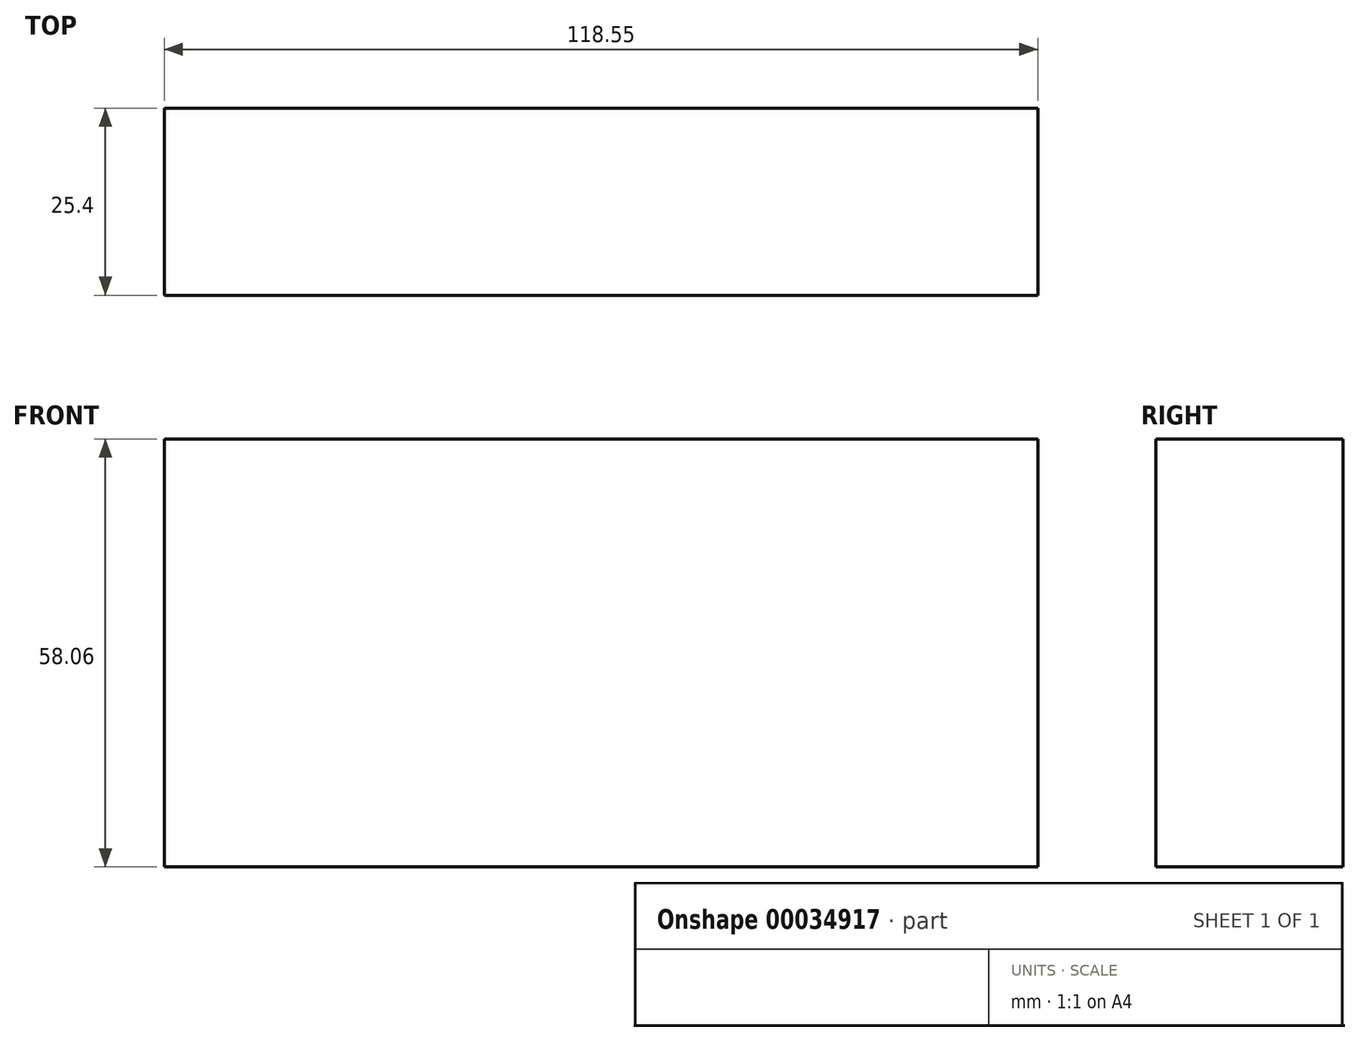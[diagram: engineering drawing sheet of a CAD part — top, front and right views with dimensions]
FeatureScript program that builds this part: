
annotation { "Feature Type Name" : "Feature", "Feature Type Description" : "" }
export const myFeature = defineFeature(function(context is Context, id is Id, definition is map)
    precondition{}
    {
        {
            var Q0;
            Q0=qCreatedBy(makeId("Front.planeOp"),FACE);
            var sketch = newSketch(context, id + "F0", { "sketchPlane" : qUnion([Q0])});
            skLineSegment(sketch, "E0.bottom", {"start": v(-55.41, 34.59) * mm, "end": v(63.14, 34.59) * mm});
            skLineSegment(sketch, "E0.top", {"start": v(-55.41, -23.47) * mm, "end": v(63.14, -23.47) * mm});
            skLineSegment(sketch, "E0.left", {"start": v(-55.41, 34.59) * mm, "end": v(-55.41, -23.47) * mm});
            skLineSegment(sketch, "E0.right", {"start": v(63.14, 34.59) * mm, "end": v(63.14, -23.47) * mm});
            skSolve(sketch);
        }
        {
            var Q0;
            Q0 = qSketchRegion(id + "F0", true);
            extrude(context, id + "F1", {"entities" : qUnion([Q0]), "depth" : 25.4 * mm});
        }
    });
